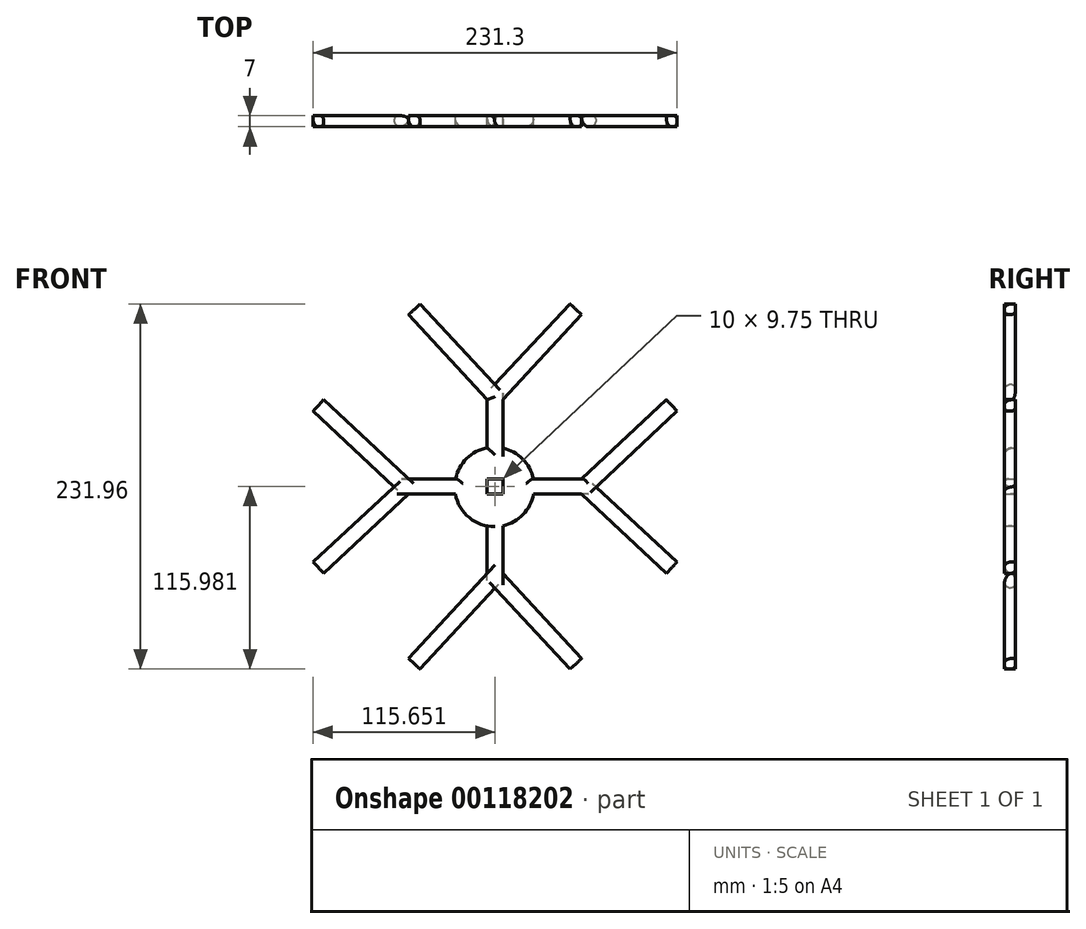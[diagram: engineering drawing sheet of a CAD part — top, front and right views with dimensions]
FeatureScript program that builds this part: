
annotation { "Feature Type Name" : "Feature", "Feature Type Description" : "" }
export const myFeature = defineFeature(function(context is Context, id is Id, definition is map)
    precondition{}
    {
        {
            var Q0;
            Q0=qCreatedBy(makeId("Front.planeOp"),FACE);
            var sketch = newSketch(context, id + "F0", { "sketchPlane" : qUnion([Q0])});
            skCircle(sketch, "E0", {"center": v(0, 0) * mm, "radius": 25.24 * mm});
            skLineSegment(sketch, "E1.bottom", {"start": v(-4.6, 55.4) * mm, "end": v(5.4, 55.4) * mm});
            skLineSegment(sketch, "E1.top", {"start": v(-4.6, -54.86) * mm, "end": v(5.4, -54.86) * mm});
            skLineSegment(sketch, "E1.left", {"start": v(-4.6, 55.4) * mm, "end": v(-4.6, -54.86) * mm});
            skLineSegment(sketch, "E1.right", {"start": v(5.4, 55.4) * mm, "end": v(5.4, -54.86) * mm});
            skLineSegment(sketch, "E2.bottom", {"start": v(-54.6, -4.6) * mm, "end": v(55.4, -4.6) * mm});
            skLineSegment(sketch, "E2.top", {"start": v(-54.6, 0) * mm, "end": v(55.4, 0) * mm});
            skLineSegment(sketch, "E2.left", {"start": v(-54.6, 0) * mm, "end": v(-54.6, -4.6) * mm});
            skLineSegment(sketch, "E2.right", {"start": v(55.4, 0) * mm, "end": v(55.4, -4.6) * mm});
            skLineSegment(sketch, "E3.top", {"start": v(-54.6, 5.15) * mm, "end": v(55.4, 5.15) * mm});
            skLineSegment(sketch, "E3.left", {"start": v(-54.6, 0) * mm, "end": v(-54.6, 5.15) * mm});
            skLineSegment(sketch, "E3.right", {"start": v(55.4, 0) * mm, "end": v(55.4, 5.15) * mm});
            skLineSegment(sketch, "E4", {"start": v(5.4, 55.4) * mm, "end": v(55.4, 109.46) * mm});
            skLineSegment(sketch, "E5", {"start": v(-4.6, 55.4) * mm, "end": v(-54.6, 109.46) * mm});
            skLineSegment(sketch, "E6", {"start": v(-4.6, -54.86) * mm, "end": v(-54.6, -108.92) * mm});
            skLineSegment(sketch, "E7", {"start": v(5.4, -54.86) * mm, "end": v(55.4, -108.92) * mm});
            skLineSegment(sketch, "E8", {"start": v(55.4, -4.6) * mm, "end": v(109.22, -54.86) * mm});
            skLineSegment(sketch, "E9", {"start": v(55.4, 5.15) * mm, "end": v(109.22, 55.4) * mm});
            skLineSegment(sketch, "E10", {"start": v(-54.6, 5.15) * mm, "end": v(-108.42, 55.4) * mm});
            skLineSegment(sketch, "E11", {"start": v(-54.6, -4.6) * mm, "end": v(-108.42, -54.86) * mm});
            skLineSegment(sketch, "E12", {"start": v(-54.6, 109.46) * mm, "end": v(-47.26, 116.25) * mm});
            skLineSegment(sketch, "E13", {"start": v(55.4, 109.46) * mm, "end": v(48.06, 116.25) * mm});
            skLineSegment(sketch, "E14", {"start": v(-47.26, 116.25) * mm, "end": v(0, 65.16) * mm});
            skLineSegment(sketch, "E15", {"start": v(0, 65.16) * mm, "end": v(48.06, 116.25) * mm});
            skLineSegment(sketch, "E16", {"start": v(-108.42, 55.4) * mm, "end": v(-115.25, 48.1) * mm});
            skLineSegment(sketch, "E17", {"start": v(-108.42, -54.86) * mm, "end": v(-115.25, -47.55) * mm});
            skLineSegment(sketch, "E18", {"start": v(-115.25, 48.1) * mm, "end": v(-63.74, 0) * mm});
            skLineSegment(sketch, "E19", {"start": v(-63.74, 0) * mm, "end": v(-115.25, -47.55) * mm});
            skLineSegment(sketch, "E20", {"start": v(55.4, -108.92) * mm, "end": v(48.06, -115.7) * mm});
            skLineSegment(sketch, "E21", {"start": v(-54.6, -108.92) * mm, "end": v(-47.26, -115.7) * mm});
            skLineSegment(sketch, "E22", {"start": v(-47.26, -115.7) * mm, "end": v(0.4, -64.18) * mm});
            skPoint(sketch, "E22.endSnap0", {"position": v(0.4, -54.86) * mm});
            skLineSegment(sketch, "E23", {"start": v(0.4, -64.18) * mm, "end": v(48.06, -115.7) * mm});
            skLineSegment(sketch, "E24", {"start": v(109.22, -54.86) * mm, "end": v(116.05, -47.55) * mm});
            skLineSegment(sketch, "E25", {"start": v(109.22, 55.4) * mm, "end": v(116.05, 48.1) * mm});
            skLineSegment(sketch, "E26", {"start": v(116.05, 48.1) * mm, "end": v(64.54, 0) * mm});
            skLineSegment(sketch, "E27", {"start": v(64.54, 0) * mm, "end": v(116.05, -47.55) * mm});
            skSolve(sketch);
        }
        {
            var Q0;
            Q0 = qSketchRegion(id + "F0", true);
            extrude(context, id + "F1", {"entities" : qUnion([Q0]), "depth" : 7 * mm});
        }
        {
            var Q0;
            {var subQ0=sQuery(id+"F0.wireOp",EDGE,"E0");Q0=makeQuery(id+"F1.opExtrude","CAP_EDGE",EDGE,{"disambiguationData":[OSD([subQ0]),TDD([makeQuery(id+"F0.imprint","IMPRINT",EDGE,{"disambiguationData":[TD([[makeQuery(id+"F0.imprint","INTERSECT",VERTEX,{"disambiguationData":[OD(0.0)],"derivedFrom":[subQ0,sQuery(id+"F0.wireOp",EDGE,"E1.left")]}),-1.0]])],"derivedFrom":subQ0})])],"isStart":false});}
            var Q1;
            {var subQ0=sQuery(id+"F0.wireOp",EDGE,"E0");Q1=makeQuery(id+"F1.opExtrude","CAP_EDGE",EDGE,{"disambiguationData":[OSD([subQ0]),TDD([makeQuery(id+"F0.imprint","IMPRINT",EDGE,{"disambiguationData":[TD([[makeQuery(id+"F0.imprint","INTERSECT",VERTEX,{"disambiguationData":[OD(0.0)],"derivedFrom":[subQ0,sQuery(id+"F0.wireOp",EDGE,"E3.top")]}),-1.0]])],"derivedFrom":subQ0})])],"isStart":false});}
            var Q2;
            {var subQ0=sQuery(id+"F0.wireOp",EDGE,"E0");Q2=makeQuery(id+"F1.opExtrude","CAP_EDGE",EDGE,{"disambiguationData":[OSD([subQ0]),TDD([makeQuery(id+"F0.imprint","IMPRINT",EDGE,{"disambiguationData":[TD([[makeQuery(id+"F0.imprint","INTERSECT",VERTEX,{"disambiguationData":[OD(0.0)],"derivedFrom":[subQ0,sQuery(id+"F0.wireOp",EDGE,"E2.bottom")]}),-1.0]])],"derivedFrom":subQ0})])],"isStart":false});}
            var Q3;
            {var subQ0=sQuery(id+"F0.wireOp",EDGE,"E0");Q3=makeQuery(id+"F1.opExtrude","CAP_EDGE",EDGE,{"disambiguationData":[OSD([subQ0]),TDD([makeQuery(id+"F0.imprint","IMPRINT",EDGE,{"disambiguationData":[TD([[makeQuery(id+"F0.imprint","INTERSECT",VERTEX,{"disambiguationData":[OD(1.0)],"derivedFrom":[subQ0,sQuery(id+"F0.wireOp",EDGE,"E1.right")]}),-1.0]])],"derivedFrom":subQ0})])],"isStart":false});}
            fillet(context, id + "F2", {"entities" : qUnion([Q0, Q1, Q2, Q3]), "radius" : 5 * mm, "tangentPropagation" : true, "allowEdgeOverflow" : false});
        }
        {
            var Q0;
            Q0=makeQuery(id+"F1.opExtrude","CAP_EDGE",EDGE,{"disambiguationData":[OSD([sQuery(id+"F0.wireOp",EDGE,"E11")])],"isStart":false});
            var Q1;
            Q1=makeQuery(id+"F1.opExtrude","CAP_EDGE",EDGE,{"disambiguationData":[OSD([sQuery(id+"F0.wireOp",EDGE,"E18")])],"isStart":false});
            var Q2;
            Q2=makeQuery(id+"F1.opExtrude","CAP_EDGE",EDGE,{"disambiguationData":[OSD([sQuery(id+"F0.wireOp",EDGE,"E5")])],"isStart":false});
            var Q3;
            Q3=makeQuery(id+"F1.opExtrude","CAP_EDGE",EDGE,{"disambiguationData":[OSD([sQuery(id+"F0.wireOp",EDGE,"E15")])],"isStart":false});
            var Q4;
            Q4=makeQuery(id+"F1.opExtrude","CAP_EDGE",EDGE,{"disambiguationData":[OSD([sQuery(id+"F0.wireOp",EDGE,"E9")])],"isStart":false});
            var Q5;
            Q5=makeQuery(id+"F1.opExtrude","CAP_EDGE",EDGE,{"disambiguationData":[OSD([sQuery(id+"F0.wireOp",EDGE,"E27")])],"isStart":false});
            var Q6;
            Q6=makeQuery(id+"F1.opExtrude","CAP_EDGE",EDGE,{"disambiguationData":[OSD([sQuery(id+"F0.wireOp",EDGE,"E7")])],"isStart":false});
            var Q7;
            Q7=makeQuery(id+"F1.opExtrude","CAP_EDGE",EDGE,{"disambiguationData":[OSD([sQuery(id+"F0.wireOp",EDGE,"E22")])],"isStart":false});
            fillet(context, id + "F3", {"entities" : qUnion([Q0, Q1, Q2, Q3, Q4, Q5, Q6, Q7]), "radius" : 5 * mm, "tangentPropagation" : true, "allowEdgeOverflow" : false});
        }
        {
            var Q0;
            Q0=makeQuery(id+"F1.opExtrude","CAP_EDGE",EDGE,{"disambiguationData":[OSD([sQuery(id+"F0.wireOp",EDGE,"E4")])],"isStart":true});
            var Q1;
            Q1=makeQuery(id+"F1.opExtrude","CAP_EDGE",EDGE,{"disambiguationData":[OSD([sQuery(id+"F0.wireOp",EDGE,"E14")])],"isStart":true});
            var Q2;
            Q2=makeQuery(id+"F1.opExtrude","CAP_EDGE",EDGE,{"disambiguationData":[OSD([sQuery(id+"F0.wireOp",EDGE,"E26")])],"isStart":true});
            var Q3;
            Q3=makeQuery(id+"F1.opExtrude","CAP_EDGE",EDGE,{"disambiguationData":[OSD([sQuery(id+"F0.wireOp",EDGE,"E8")])],"isStart":true});
            var Q4;
            Q4=makeQuery(id+"F1.opExtrude","CAP_EDGE",EDGE,{"disambiguationData":[OSD([sQuery(id+"F0.wireOp",EDGE,"E23")])],"isStart":true});
            var Q5;
            Q5=makeQuery(id+"F1.opExtrude","CAP_EDGE",EDGE,{"disambiguationData":[OSD([sQuery(id+"F0.wireOp",EDGE,"E6")])],"isStart":true});
            var Q6;
            Q6=makeQuery(id+"F1.opExtrude","CAP_EDGE",EDGE,{"disambiguationData":[OSD([sQuery(id+"F0.wireOp",EDGE,"E19")])],"isStart":true});
            var Q7;
            Q7=makeQuery(id+"F1.opExtrude","CAP_EDGE",EDGE,{"disambiguationData":[OSD([sQuery(id+"F0.wireOp",EDGE,"E10")])],"isStart":true});
            fillet(context, id + "F4", {"entities" : qUnion([Q0, Q1, Q2, Q3, Q4, Q5, Q6, Q7]), "radius" : 3 * mm, "tangentPropagation" : true, "allowEdgeOverflow" : false});
        }
        {
            var Q0;
            {var subQ0=sQuery(id+"F0.wireOp",EDGE,"E1.left");Q0=makeQuery(id+"F1.opExtrude","CAP_EDGE",EDGE,{"disambiguationData":[OSD([subQ0]),TDD([makeQuery(id+"F0.imprint","IMPRINT",EDGE,{"disambiguationData":[TD([[makeQuery(id+"F0.imprint","INTERSECT",VERTEX,{"disambiguationData":[OD(0.0)],"derivedFrom":[sQuery(id+"F0.wireOp",EDGE,"E0"),subQ0]}),1.0]])],"derivedFrom":subQ0})])],"isStart":false});}
            var Q1;
            {var subQ0=sQuery(id+"F0.wireOp",EDGE,"E1.right");Q1=makeQuery(id+"F1.opExtrude","CAP_EDGE",EDGE,{"disambiguationData":[OSD([subQ0]),TDD([makeQuery(id+"F0.imprint","IMPRINT",EDGE,{"disambiguationData":[TD([[makeQuery(id+"F0.imprint","INTERSECT",VERTEX,{"disambiguationData":[OD(0.0)],"derivedFrom":[sQuery(id+"F0.wireOp",EDGE,"E0"),subQ0]}),1.0]])],"derivedFrom":subQ0})])],"isStart":false});}
            fillet(context, id + "F5", {"entities" : qUnion([Q0, Q1]), "radius" : 5 * mm, "tangentPropagation" : true, "allowEdgeOverflow" : false});
        }
        {
            var Q0;
            {var subQ0=sQuery(id+"F0.wireOp",EDGE,"E1.right");Q0=makeQuery(id+"F1.opExtrude","CAP_EDGE",EDGE,{"disambiguationData":[OSD([subQ0]),TDD([makeQuery(id+"F0.imprint","IMPRINT",EDGE,{"disambiguationData":[TD([[makeQuery(id+"F0.imprint","INTERSECT",VERTEX,{"disambiguationData":[OD(1.0)],"derivedFrom":[sQuery(id+"F0.wireOp",EDGE,"E0"),subQ0]}),-1.0]])],"derivedFrom":subQ0})])],"isStart":false});}
            var Q1;
            {var subQ0=sQuery(id+"F0.wireOp",EDGE,"E1.left");Q1=makeQuery(id+"F1.opExtrude","CAP_EDGE",EDGE,{"disambiguationData":[OSD([subQ0]),TDD([makeQuery(id+"F0.imprint","IMPRINT",EDGE,{"disambiguationData":[TD([[makeQuery(id+"F0.imprint","INTERSECT",VERTEX,{"disambiguationData":[OD(1.0)],"derivedFrom":[sQuery(id+"F0.wireOp",EDGE,"E0"),subQ0]}),-1.0]])],"derivedFrom":subQ0})])],"isStart":false});}
            fillet(context, id + "F6", {"entities" : qUnion([Q0, Q1]), "radius" : 5 * mm, "tangentPropagation" : true, "allowEdgeOverflow" : false});
        }
        {
            var Q0;
            {var subQ0=sQuery(id+"F0.wireOp",EDGE,"E2.bottom");Q0=makeQuery(id+"F1.opExtrude","CAP_EDGE",EDGE,{"disambiguationData":[OSD([subQ0]),TDD([makeQuery(id+"F0.imprint","IMPRINT",EDGE,{"disambiguationData":[TD([[makeQuery(id+"F0.imprint","INTERSECT",VERTEX,{"disambiguationData":[OD(0.0)],"derivedFrom":[sQuery(id+"F0.wireOp",EDGE,"E0"),subQ0]}),1.0]])],"derivedFrom":subQ0})])],"isStart":false});}
            var Q1;
            {var subQ0=sQuery(id+"F0.wireOp",EDGE,"E3.top");Q1=makeQuery(id+"F1.opExtrude","CAP_EDGE",EDGE,{"disambiguationData":[OSD([subQ0]),TDD([makeQuery(id+"F0.imprint","IMPRINT",EDGE,{"disambiguationData":[TD([[makeQuery(id+"F0.imprint","INTERSECT",VERTEX,{"disambiguationData":[OD(1.0)],"derivedFrom":[sQuery(id+"F0.wireOp",EDGE,"E0"),subQ0]}),1.0]])],"derivedFrom":subQ0})])],"isStart":false});}
            var Q2;
            {var subQ0=sQuery(id+"F0.wireOp",EDGE,"E2.bottom");Q2=makeQuery(id+"F1.opExtrude","CAP_EDGE",EDGE,{"disambiguationData":[OSD([subQ0]),TDD([makeQuery(id+"F0.imprint","IMPRINT",EDGE,{"disambiguationData":[TD([[makeQuery(id+"F0.imprint","INTERSECT",VERTEX,{"disambiguationData":[OD(1.0)],"derivedFrom":[sQuery(id+"F0.wireOp",EDGE,"E0"),subQ0]}),-1.0]])],"derivedFrom":subQ0})])],"isStart":false});}
            var Q3;
            {var subQ0=sQuery(id+"F0.wireOp",EDGE,"E3.top");Q3=makeQuery(id+"F1.opExtrude","CAP_EDGE",EDGE,{"disambiguationData":[OSD([subQ0]),TDD([makeQuery(id+"F0.imprint","IMPRINT",EDGE,{"disambiguationData":[TD([[makeQuery(id+"F0.imprint","INTERSECT",VERTEX,{"disambiguationData":[OD(0.0)],"derivedFrom":[sQuery(id+"F0.wireOp",EDGE,"E0"),subQ0]}),-1.0]])],"derivedFrom":subQ0})])],"isStart":false});}
            fillet(context, id + "F7", {"entities" : qUnion([Q0, Q1, Q2, Q3]), "radius" : 3 * mm, "tangentPropagation" : true, "allowEdgeOverflow" : false});
        }
    });
